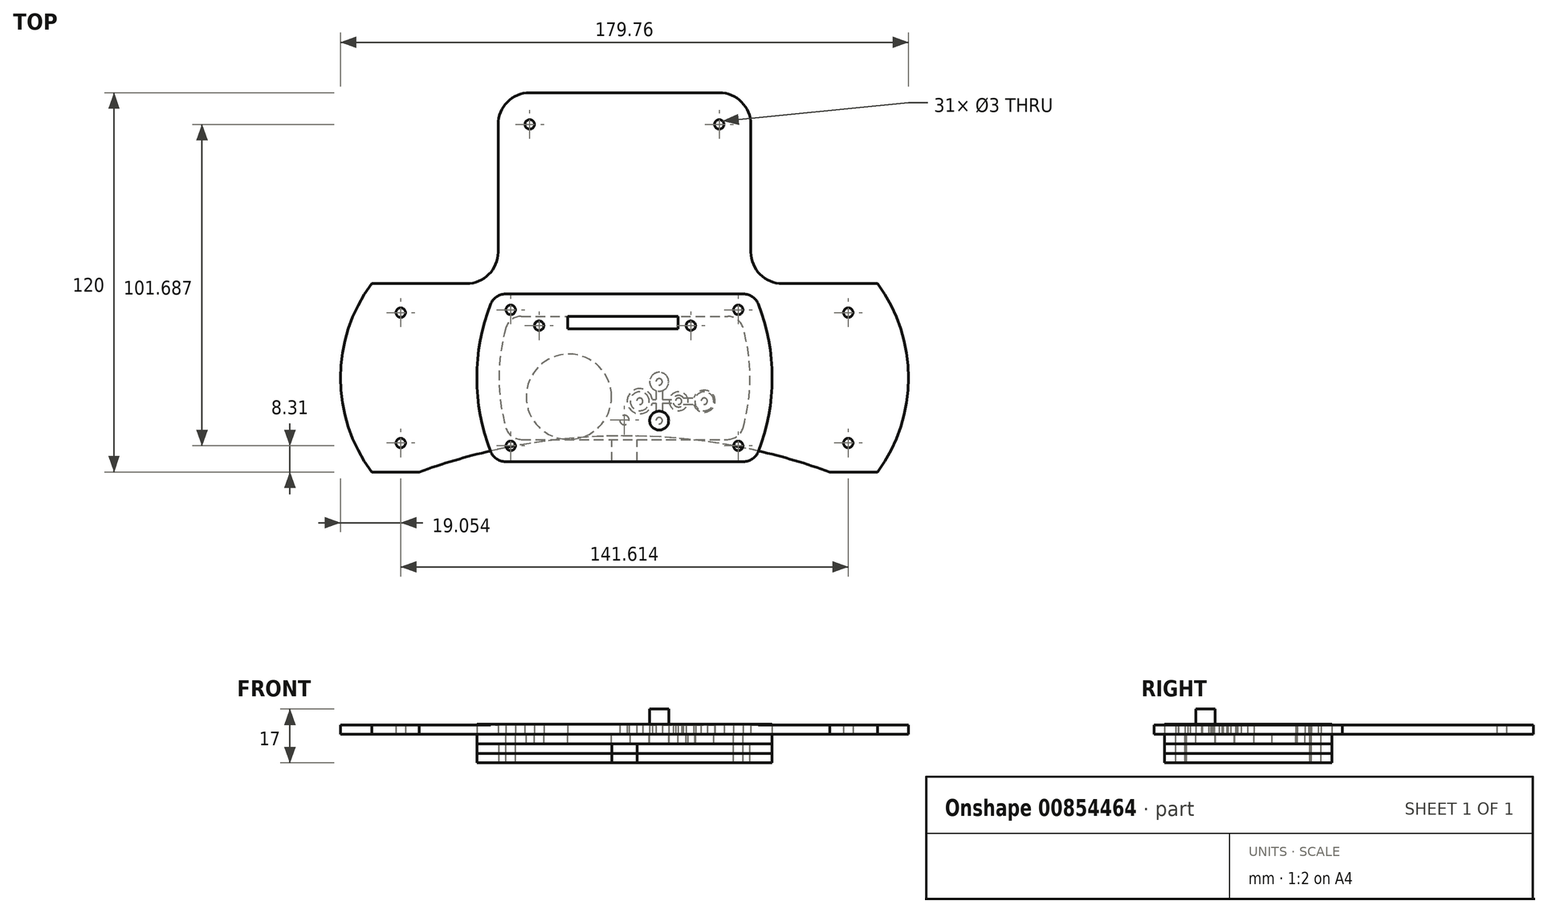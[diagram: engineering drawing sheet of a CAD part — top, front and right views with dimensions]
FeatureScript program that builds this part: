
annotation { "Feature Type Name" : "Feature", "Feature Type Description" : "" }
export const myFeature = defineFeature(function(context is Context, id is Id, definition is map)
    precondition{}
    {
        {
            var Q0;
            Q0=qCreatedBy(makeId("Top.planeOp"),FACE);
            var sketch = newSketch(context, id + "F0", { "sketchPlane" : qUnion([Q0])});
            skLineSegment(sketch, "E0.bottom", {"start": v(80.04, -29.81) * mm, "end": v(65, -29.81) * mm});
            skLineSegment(sketch, "E0.top", {"start": v(80.04, 29.81) * mm, "end": v(50, 29.81) * mm});
            skPoint(sketch, "E0.middle", {"position": v(0, 0) * mm});
            skLineSegment(sketch, "E1.top", {"start": v(30, 90.19) * mm, "end": v(-30, 90.19) * mm});
            skLineSegment(sketch, "E1.left", {"start": v(40, 39.81) * mm, "end": v(40, 80.19) * mm});
            skLineSegment(sketch, "E1.right", {"start": v(-40, 39.81) * mm, "end": v(-40, 80.19) * mm});
            skPoint(sketch, "E1.middle", {"position": v(0, 60) * mm});
            skPoint(sketch, "E2.visualSharp", {"position": v(-40, 29.81) * mm});
            skPoint(sketch, "E3.visualSharp", {"position": v(-40, 90.19) * mm});
            skPoint(sketch, "E4.visualSharp", {"position": v(40, 90.19) * mm});
            skPoint(sketch, "E5.visualSharp", {"position": v(40, 29.81) * mm});
            skPoint(sketch, "E6.visualSharp", {"position": v(80, 29.81) * mm});
            skPoint(sketch, "E7", {"position": v(-65, -29.81) * mm});
            skPoint(sketch, "E8", {"position": v(65, -29.81) * mm});
            skArc(sketch, "E9", {"start": v(65, -29.81) * mm, "mid": v(0, -18.35) * mm, "end": v(-65, -29.81) * mm});
            skPoint(sketch, "E10.visualSharp", {"position": v(-80, -29.81) * mm});
            skPoint(sketch, "E11.visualSharp", {"position": v(80, -29.81) * mm});
            skPoint(sketch, "E12.visualSharp", {"position": v(-80, 29.81) * mm});
            skLineSegment(sketch, "E13.trimOffspring", {"start": v(-65, -29.81) * mm, "end": v(-80, -29.81) * mm});
            skLineSegment(sketch, "E14.trimOffspring", {"start": v(-50, 29.81) * mm, "end": v(-80, 29.81) * mm});
            skArc(sketch, "E15.filletArc", {"start": v(-50, 29.81) * mm, "mid": v(-42.93, 32.74) * mm, "end": v(-40, 39.81) * mm});
            skArc(sketch, "E16.filletArc", {"start": v(40, 39.81) * mm, "mid": v(42.93, 32.74) * mm, "end": v(50, 29.81) * mm});
            skArc(sketch, "E17.filletArc", {"start": v(-30, 90.19) * mm, "mid": v(-37.07, 87.26) * mm, "end": v(-40, 80.19) * mm});
            skArc(sketch, "E18.filletArc", {"start": v(40, 80.19) * mm, "mid": v(37.07, 87.26) * mm, "end": v(30, 90.19) * mm});
            skArc(sketch, "E19", {"start": v(-80, 29.81) * mm, "mid": v(-89.86, 0) * mm, "end": v(-80, -29.81) * mm});
            skArc(sketch, "E20.MirrorCS", {"start": v(80, 29.87) * mm, "mid": v(89.9, 0) * mm, "end": v(80, -29.87) * mm});
            skLineSegment(sketch, "E21", {"start": v(0, 90.19) * mm, "end": v(0, 0) * mm, "construction": true});
            skCircle(sketch, "E22", {"center": v(-30, 80.19) * mm, "radius": 1.5 * mm});
            skCircle(sketch, "E23", {"center": v(30, 80.19) * mm, "radius": 1.5 * mm});
            skCircle(sketch, "E24", {"center": v(-70.8, 20.62) * mm, "radius": 1.5 * mm});
            skLineSegment(sketch, "E25", {"start": v(-80, 29.81) * mm, "end": v(-70.8, 20.62) * mm, "construction": true});
            skLineSegment(sketch, "E26.MirrorCS", {"start": v(80, 29.81) * mm, "end": v(70.8, 20.62) * mm, "construction": true});
            skCircle(sketch, "E27.MirrorC", {"center": v(70.8, 20.62) * mm, "radius": 1.5 * mm});
            skLineSegment(sketch, "E28", {"start": v(0, 0) * mm, "end": v(-39.86, 0) * mm, "construction": true});
            skLineSegment(sketch, "E29.MirrorCS", {"start": v(0, 0) * mm, "end": v(39.86, 0) * mm, "construction": true});
            skLineSegment(sketch, "E30.MirrorCS", {"start": v(80, -29.8) * mm, "end": v(70.8, -20.61) * mm, "construction": true});
            skCircle(sketch, "E31.MirrorC", {"center": v(70.8, -20.61) * mm, "radius": 1.5 * mm});
            skLineSegment(sketch, "E32.MirrorCS", {"start": v(-80, -29.82) * mm, "end": v(-70.8, -20.63) * mm, "construction": true});
            skCircle(sketch, "E33.MirrorC", {"center": v(-70.8, -20.63) * mm, "radius": 1.5 * mm});
            skLineSegment(sketch, "E34", {"start": v(0, -18.35) * mm, "end": v(0, -13.35) * mm, "construction": true});
            skCircle(sketch, "E35", {"center": v(0, -13.35) * mm, "radius": 1.5 * mm});
            skSolve(sketch);
        }
        {
            var Q0;
            Q0=qCreatedBy(makeId("Top.planeOp"),FACE);
            var sketch = newSketch(context, id + "F1", { "sketchPlane" : qUnion([Q0])});
            skLineSegment(sketch, "E36.bottom", {"start": v(36, -21.5) * mm, "end": v(-36, -21.5) * mm, "construction": true});
            skLineSegment(sketch, "E36.top", {"start": v(36, 21.5) * mm, "end": v(-36, 21.5) * mm, "construction": true});
            skLineSegment(sketch, "E36.left", {"start": v(36, -21.5) * mm, "end": v(36, 21.5) * mm, "construction": true});
            skLineSegment(sketch, "E36.right", {"start": v(-36, -21.5) * mm, "end": v(-36, 21.5) * mm, "construction": true});
            skPoint(sketch, "E36.middle", {"position": v(0, 0) * mm});
            skLineSegment(sketch, "E37", {"start": v(-36, -6) * mm, "end": v(-17.6, -6) * mm, "construction": true});
            skLineSegment(sketch, "E38", {"start": v(-17.6, -6) * mm, "end": v(-17.6, -21.5) * mm, "construction": true});
            skCircle(sketch, "E39", {"center": v(-17.6, -6) * mm, "radius": 13.5 * mm});
            skCircle(sketch, "E40", {"center": v(4.84, -7.4) * mm, "radius": 3 * mm});
            skCircle(sketch, "E41", {"center": v(17.14, -7.4) * mm, "radius": 3 * mm});
            skCircle(sketch, "E42", {"center": v(10.99, -13.55) * mm, "radius": 3 * mm});
            skCircle(sketch, "E43", {"center": v(25.23, -7.4) * mm, "radius": 3 * mm});
            skCircle(sketch, "E44", {"center": v(10.99, -1.25) * mm, "radius": 3 * mm});
            skLineSegment(sketch, "E45", {"start": v(4.84, -7.4) * mm, "end": v(17.14, -7.4) * mm, "construction": true});
            skLineSegment(sketch, "E46", {"start": v(10.99, -1.25) * mm, "end": v(10.99, -13.55) * mm, "construction": true});
            skLineSegment(sketch, "E47", {"start": v(17.14, -7.4) * mm, "end": v(25.23, -7.4) * mm, "construction": true});
            skPoint(sketch, "E48", {"position": v(10.99, -7.4) * mm});
            skLineSegment(sketch, "E49.0", {"start": v(37.68, 26.5) * mm, "end": v(-37.68, 26.5) * mm});
            skLineSegment(sketch, "E49.1", {"start": v(41, -26.5) * mm, "end": v(41, 26.5) * mm, "construction": true});
            skLineSegment(sketch, "E49.2", {"start": v(37.68, -26.5) * mm, "end": v(-37.68, -26.5) * mm});
            skLineSegment(sketch, "E49.3", {"start": v(-41, -26.5) * mm, "end": v(-41, 26.5) * mm, "construction": true});
            skArc(sketch, "E50", {"start": v(42.34, -23.32) * mm, "mid": v(46.73, 0) * mm, "end": v(42.34, 23.32) * mm});
            skLineSegment(sketch, "E51", {"start": v(0, 21.5) * mm, "end": v(0, 0) * mm, "construction": true});
            skArc(sketch, "E52.MirrorCS", {"start": v(-42.34, -23.32) * mm, "mid": v(-46.73, 0) * mm, "end": v(-42.34, 23.32) * mm});
            skPoint(sketch, "E53.visualSharp", {"position": v(-41, 26.5) * mm});
            skArc(sketch, "E53.filletArc", {"start": v(-37.68, 26.5) * mm, "mid": v(-40.5, 25.63) * mm, "end": v(-42.34, 23.32) * mm});
            skPoint(sketch, "E54.visualSharp", {"position": v(41, 26.5) * mm});
            skArc(sketch, "E54.filletArc", {"start": v(42.34, 23.32) * mm, "mid": v(40.5, 25.63) * mm, "end": v(37.68, 26.5) * mm});
            skPoint(sketch, "E55.visualSharp", {"position": v(41, -26.5) * mm});
            skArc(sketch, "E55.filletArc", {"start": v(37.68, -26.5) * mm, "mid": v(40.5, -25.63) * mm, "end": v(42.34, -23.32) * mm});
            skPoint(sketch, "E56.visualSharp", {"position": v(-41, -26.5) * mm});
            skArc(sketch, "E56.filletArc", {"start": v(-42.34, -23.32) * mm, "mid": v(-40.5, -25.63) * mm, "end": v(-37.68, -26.5) * mm});
            skLineSegment(sketch, "E57", {"start": v(-27, 21.5) * mm, "end": v(-27, 16.5) * mm, "construction": true});
            skLineSegment(sketch, "E58", {"start": v(21, 21.5) * mm, "end": v(21, 16.5) * mm, "construction": true});
            skLineSegment(sketch, "E59", {"start": v(21, 16.5) * mm, "end": v(36, 16.5) * mm, "construction": true});
            skLineSegment(sketch, "E60", {"start": v(-27, 16.5) * mm, "end": v(-36, 16.5) * mm, "construction": true});
            skCircle(sketch, "E61", {"center": v(-27, 16.5) * mm, "radius": 1.5 * mm});
            skCircle(sketch, "E62", {"center": v(21, 16.5) * mm, "radius": 1.5 * mm});
            skCircle(sketch, "E63", {"center": v(-36, 21.5) * mm, "radius": 1.5 * mm});
            skCircle(sketch, "E64", {"center": v(36, 21.5) * mm, "radius": 1.5 * mm});
            skCircle(sketch, "E65", {"center": v(36, -21.5) * mm, "radius": 1.5 * mm});
            skCircle(sketch, "E66", {"center": v(-36, -21.5) * mm, "radius": 1.5 * mm});
            skLineSegment(sketch, "E67.bottom", {"start": v(-18, 19.49) * mm, "end": v(17, 19.49) * mm});
            skLineSegment(sketch, "E67.top", {"start": v(-18, 15.49) * mm, "end": v(17, 15.49) * mm});
            skLineSegment(sketch, "E67.left", {"start": v(-18, 19.49) * mm, "end": v(-18, 15.49) * mm});
            skLineSegment(sketch, "E67.right", {"start": v(17, 19.49) * mm, "end": v(17, 15.49) * mm});
            skLineSegment(sketch, "E68", {"start": v(1.84, -7.4) * mm, "end": v(-4.16, -7.4) * mm, "construction": true});
            skLineSegment(sketch, "E69", {"start": v(10.43, -16.5) * mm, "end": v(10.43, -21.5) * mm, "construction": true});
            skSolve(sketch);
        }
        {
            var Q0;
            Q0 = qSketchRegion(id + "F0", true);
            extrude(context, id + "F2", {"entities" : qUnion([Q0]), "depth" : 3 * mm, "offsetDistance" : 25 * mm});
        }
        {
            var Q0;
            Q0=makeQuery(id+"F1.imprint","IMPRINT",FACE,{"disambiguationData":[TD([[makeQuery(id+"F1.imprint","IMPRINT",EDGE,{"derivedFrom":sQuery(id+"F1.wireOp",EDGE,"E39")}),-1.0]])]});
            extrude(context, id + "F3", {"entities" : qUnion([Q0]), "oppositeDirection" : true, "depth" : 3 * mm, "offsetDistance" : 25 * mm});
        }
        {
            var Q0;
            Q0=makeQuery(id+"F3.opExtrude","CAP_FACE",FACE,{"disambiguationData":[OSD([sQuery(id+"F1.wireOp",EDGE,"E39"),sQuery(id+"F1.wireOp",EDGE,"E40"),sQuery(id+"F1.wireOp",EDGE,"E41"),sQuery(id+"F1.wireOp",EDGE,"E42"),sQuery(id+"F1.wireOp",EDGE,"E43"),sQuery(id+"F1.wireOp",EDGE,"E44"),sQuery(id+"F1.wireOp",EDGE,"E49.0"),sQuery(id+"F1.wireOp",EDGE,"E49.2"),sQuery(id+"F1.wireOp",EDGE,"E50"),sQuery(id+"F1.wireOp",EDGE,"E52.MirrorCS"),sQuery(id+"F1.wireOp",EDGE,"E53.filletArc"),sQuery(id+"F1.wireOp",EDGE,"E54.filletArc"),sQuery(id+"F1.wireOp",EDGE,"E55.filletArc"),sQuery(id+"F1.wireOp",EDGE,"E56.filletArc"),sQuery(id+"F1.wireOp",EDGE,"E61"),sQuery(id+"F1.wireOp",EDGE,"E62"),sQuery(id+"F1.wireOp",EDGE,"E63"),sQuery(id+"F1.wireOp",EDGE,"E64"),sQuery(id+"F1.wireOp",EDGE,"E65"),sQuery(id+"F1.wireOp",EDGE,"E66")])],"isStart":false});
            var sketch = newSketch(context, id + "F4", { "sketchPlane" : qUnion([Q0])});
            skLineSegment(sketch, "E70", {"start": v(-37.68, -26.5) * mm, "end": v(37.68, -26.5) * mm});
            skArc(sketch, "E71", {"start": v(37.68, -26.5) * mm, "mid": v(40.5, -25.63) * mm, "end": v(42.34, -23.32) * mm});
            skArc(sketch, "E72", {"start": v(42.34, 23.32) * mm, "mid": v(40.5, 25.63) * mm, "end": v(37.68, 26.5) * mm});
            skArc(sketch, "E73", {"start": v(42.34, -23.32) * mm, "mid": v(46.73, 0) * mm, "end": v(42.34, 23.32) * mm});
            skLineSegment(sketch, "E74", {"start": v(0, 26.5) * mm, "end": v(0, 0) * mm, "construction": true});
            skArc(sketch, "E75.MirrorCS", {"start": v(-42.34, -23.32) * mm, "mid": v(-46.73, 0) * mm, "end": v(-42.34, 23.32) * mm});
            skArc(sketch, "E76.MirrorCS", {"start": v(-42.34, 23.32) * mm, "mid": v(-40.5, 25.63) * mm, "end": v(-37.68, 26.5) * mm});
            skArc(sketch, "E77.MirrorCS", {"start": v(-37.68, -26.5) * mm, "mid": v(-40.5, -25.63) * mm, "end": v(-42.34, -23.32) * mm});
            skArc(sketch, "E78.1", {"start": v(-37.48, -15.9) * mm, "mid": v(-39.73, 0) * mm, "end": v(-37.48, 15.9) * mm});
            skLineSegment(sketch, "E78.2", {"start": v(-32.67, -19.5) * mm, "end": v(32.67, -19.5) * mm});
            skArc(sketch, "E78.3", {"start": v(37.48, -15.9) * mm, "mid": v(39.73, 0) * mm, "end": v(37.48, 15.9) * mm});
            skPoint(sketch, "E79.visualSharp", {"position": v(-36.3, 19.5) * mm});
            skArc(sketch, "E79.filletArc", {"start": v(-32.67, 19.5) * mm, "mid": v(-35.68, 18.5) * mm, "end": v(-37.48, 15.9) * mm});
            skPoint(sketch, "E80.visualSharp", {"position": v(36.3, 19.5) * mm});
            skArc(sketch, "E80.filletArc", {"start": v(37.48, 15.9) * mm, "mid": v(35.68, 18.5) * mm, "end": v(32.67, 19.5) * mm});
            skPoint(sketch, "E81.visualSharp", {"position": v(-36.3, -19.5) * mm});
            skArc(sketch, "E81.filletArc", {"start": v(-37.48, -15.9) * mm, "mid": v(-35.68, -18.5) * mm, "end": v(-32.67, -19.5) * mm});
            skPoint(sketch, "E82.visualSharp", {"position": v(36.3, -19.5) * mm});
            skArc(sketch, "E82.filletArc", {"start": v(32.67, -19.5) * mm, "mid": v(35.68, -18.5) * mm, "end": v(37.48, -15.9) * mm});
            skCircle(sketch, "E83", {"center": v(-36, 21.5) * mm, "radius": 1.5 * mm});
            skCircle(sketch, "E84", {"center": v(36, 21.5) * mm, "radius": 1.5 * mm});
            skCircle(sketch, "E85", {"center": v(36, -21.5) * mm, "radius": 1.5 * mm});
            skCircle(sketch, "E86", {"center": v(-36, -21.5) * mm, "radius": 1.5 * mm});
            skLineSegment(sketch, "E87", {"start": v(-4, 26.5) * mm, "end": v(-4, 19.5) * mm});
            skLineSegment(sketch, "E88.MirrorCS", {"start": v(4, 26.5) * mm, "end": v(4, 19.5) * mm});
            skLineSegment(sketch, "E89.trimOffspring", {"start": v(4, 26.5) * mm, "end": v(37.68, 26.5) * mm});
            skLineSegment(sketch, "E90.trimOffspring", {"start": v(4, 19.5) * mm, "end": v(32.67, 19.5) * mm});
            skLineSegment(sketch, "E91", {"start": v(-37.68, 26.5) * mm, "end": v(-4, 26.5) * mm});
            skLineSegment(sketch, "E92", {"start": v(-32.67, 19.5) * mm, "end": v(-4, 19.5) * mm});
            skLineSegment(sketch, "E93", {"start": v(-4, 19.5) * mm, "end": v(4, 19.5) * mm});
            skLineSegment(sketch, "E94", {"start": v(-4, 26.5) * mm, "end": v(4, 26.5) * mm});
            skSolve(sketch);
        }
        {
            var Q0;
            Q0=makeQuery(id+"F4.imprint","IMPRINT",FACE,{"disambiguationData":[TD([[makeQuery(id+"F4.imprint","IMPRINT",EDGE,{"derivedFrom":sQuery(id+"F4.wireOp",EDGE,"E70")}),-1.0]])]});
            extrude(context, id + "F5", {"entities" : qUnion([Q0]), "depth" : 3 * mm, "offsetDistance" : 25 * mm});
        }
        {
            var Q0;
            Q0=makeQuery(id+"F1.imprint","IMPRINT",FACE,{"disambiguationData":[TD([[makeQuery(id+"F1.imprint","IMPRINT",EDGE,{"derivedFrom":sQuery(id+"F1.wireOp",EDGE,"E39")}),-1.0]])]});
            var sketch = newSketch(context, id + "F6", { "sketchPlane" : qUnion([Q0])});
            skArc(sketch, "E95", {"start": v(11.99, -4.08) * mm, "mid": v(10.99, 1.75) * mm, "end": v(9.99, -4.08) * mm});
            skArc(sketch, "E96", {"start": v(8.77, -6.8) * mm, "mid": v(0.85, -7.4) * mm, "end": v(8.77, -8.01) * mm});
            skArc(sketch, "E97", {"start": v(9.99, -10.72) * mm, "mid": v(10.99, -16.55) * mm, "end": v(11.99, -10.72) * mm});
            skArc(sketch, "E98", {"start": v(15.41, -8.01) * mm, "mid": v(16.92, -9.21) * mm, "end": v(18.66, -8.4) * mm});
            skArc(sketch, "E99", {"start": v(21.9, -8.4) * mm, "mid": v(28.7, -7.4) * mm, "end": v(21.9, -6.4) * mm});
            skLineSegment(sketch, "E100.0", {"start": v(8.77, -8.01) * mm, "end": v(9.99, -8.01) * mm});
            skLineSegment(sketch, "E101.0", {"start": v(9.99, -4.08) * mm, "end": v(9.99, -6.8) * mm});
            skLineSegment(sketch, "E102.MirrorCS", {"start": v(11.99, -4.08) * mm, "end": v(11.99, -6.8) * mm});
            skLineSegment(sketch, "E103.MirrorCS", {"start": v(8.77, -6.8) * mm, "end": v(9.99, -6.8) * mm});
            skPoint(sketch, "E104.orphan", {"position": v(11.99, -1.25) * mm});
            skPoint(sketch, "E105.orphan", {"position": v(9.99, -1.25) * mm});
            skLineSegment(sketch, "E106.trimOffspring", {"start": v(11.99, -6.8) * mm, "end": v(15.41, -6.8) * mm});
            skLineSegment(sketch, "E107.trimOffspring", {"start": v(11.99, -8.01) * mm, "end": v(11.99, -10.72) * mm});
            skLineSegment(sketch, "E108.trimOffspring", {"start": v(9.99, -8.01) * mm, "end": v(9.99, -10.72) * mm});
            skPoint(sketch, "E109.orphan", {"position": v(18.24, -6.8) * mm});
            skPoint(sketch, "E110.orphan", {"position": v(18.24, -8.01) * mm});
            skLineSegment(sketch, "E111.trimOffspring", {"start": v(11.99, -8.01) * mm, "end": v(15.41, -8.01) * mm});
            skPoint(sketch, "E112.orphan", {"position": v(11.99, -13.55) * mm});
            skPoint(sketch, "E113.orphan", {"position": v(9.99, -13.55) * mm});
            skLineSegment(sketch, "E114.0", {"start": v(18.66, -8.4) * mm, "end": v(21.9, -8.4) * mm});
            skLineSegment(sketch, "E115.MirrorCS", {"start": v(18.66, -6.4) * mm, "end": v(21.9, -6.4) * mm});
            skPoint(sketch, "E116.orphan", {"position": v(15.83, -6.4) * mm});
            skPoint(sketch, "E117.orphan", {"position": v(15.83, -8.4) * mm});
            skArc(sketch, "E118.trimOffspring", {"start": v(18.66, -6.4) * mm, "mid": v(16.92, -5.6) * mm, "end": v(15.41, -6.8) * mm});
            skPoint(sketch, "E119.orphan", {"position": v(24.73, -6.4) * mm});
            skPoint(sketch, "E120.orphan", {"position": v(24.73, -8.4) * mm});
            skCircle(sketch, "E121", {"center": v(4.84, -7.4) * mm, "radius": 1 * mm});
            skCircle(sketch, "E122", {"center": v(10.99, -1.25) * mm, "radius": 1 * mm});
            skCircle(sketch, "E123", {"center": v(10.99, -13.55) * mm, "radius": 1 * mm});
            skCircle(sketch, "E124", {"center": v(17.14, -7.4) * mm, "radius": 1 * mm});
            skCircle(sketch, "E125", {"center": v(25.23, -7.4) * mm, "radius": 1 * mm});
            skSolve(sketch);
        }
        {
            var Q0;
            Q0 = qSketchRegion(id + "F6", true);
            extrude(context, id + "F7", {"entities" : qUnion([Q0]), "depth" : 3 * mm, "offsetDistance" : 25 * mm});
        }
        {
            var Q0;
            Q0=makeQuery(id+"F7.opExtrude","CAP_FACE",FACE,{"disambiguationData":[OSD([sQuery(id+"F6.wireOp",EDGE,"E95"),sQuery(id+"F6.wireOp",EDGE,"E96"),sQuery(id+"F6.wireOp",EDGE,"E97"),sQuery(id+"F6.wireOp",EDGE,"E98"),sQuery(id+"F6.wireOp",EDGE,"E99"),sQuery(id+"F6.wireOp",EDGE,"E100.0"),sQuery(id+"F6.wireOp",EDGE,"E101.0"),sQuery(id+"F6.wireOp",EDGE,"E102.MirrorCS"),sQuery(id+"F6.wireOp",EDGE,"E103.MirrorCS"),sQuery(id+"F6.wireOp",EDGE,"E106.trimOffspring"),sQuery(id+"F6.wireOp",EDGE,"E107.trimOffspring"),sQuery(id+"F6.wireOp",EDGE,"E108.trimOffspring"),sQuery(id+"F6.wireOp",EDGE,"E111.trimOffspring"),sQuery(id+"F6.wireOp",EDGE,"E114.0"),sQuery(id+"F6.wireOp",EDGE,"E115.MirrorCS"),sQuery(id+"F6.wireOp",EDGE,"E118.trimOffspring"),sQuery(id+"F6.wireOp",EDGE,"E121"),sQuery(id+"F6.wireOp",EDGE,"E122"),sQuery(id+"F6.wireOp",EDGE,"E123"),sQuery(id+"F6.wireOp",EDGE,"E124"),sQuery(id+"F6.wireOp",EDGE,"E125")])],"isStart":false});
            var sketch = newSketch(context, id + "F8", { "sketchPlane" : qUnion([Q0])});
            skCircle(sketch, "E126", {"center": v(10.99, -13.55) * mm, "radius": 3 * mm});
            skSolve(sketch);
        }
        {
            var Q0;
            Q0 = qSketchRegion(id + "F8", true);
            extrude(context, id + "F9", {"entities" : qUnion([Q0]), "depth" : 5 * mm, "offsetDistance" : 25 * mm});
        }
        {
            var Q0;
            Q0=makeQuery(id+"F1.imprint","IMPRINT",FACE,{"disambiguationData":[TD([[makeQuery(id+"F1.imprint","IMPRINT",EDGE,{"derivedFrom":sQuery(id+"F1.wireOp",EDGE,"E40")}),1.0]])]});
            var Q1;
            Q1=makeQuery(id+"F1.imprint","IMPRINT",FACE,{"disambiguationData":[TD([[makeQuery(id+"F1.imprint","IMPRINT",EDGE,{"derivedFrom":sQuery(id+"F1.wireOp",EDGE,"E44")}),1.0]])]});
            var Q2;
            Q2=makeQuery(id+"F1.imprint","IMPRINT",FACE,{"disambiguationData":[TD([[makeQuery(id+"F1.imprint","IMPRINT",EDGE,{"derivedFrom":sQuery(id+"F1.wireOp",EDGE,"E41")}),1.0]])]});
            var Q3;
            Q3=makeQuery(id+"F1.imprint","IMPRINT",FACE,{"disambiguationData":[TD([[makeQuery(id+"F1.imprint","IMPRINT",EDGE,{"derivedFrom":sQuery(id+"F1.wireOp",EDGE,"E42")}),1.0]])]});
            var Q4;
            Q4=makeQuery(id+"F1.imprint","IMPRINT",FACE,{"disambiguationData":[TD([[makeQuery(id+"F1.imprint","IMPRINT",EDGE,{"derivedFrom":sQuery(id+"F1.wireOp",EDGE,"E43")}),1.0]])]});
            var Q5;
            Q5=makeQuery(id+"F1.imprint","IMPRINT",FACE,{"disambiguationData":[TD([[makeQuery(id+"F1.imprint","IMPRINT",EDGE,{"derivedFrom":sQuery(id+"F1.wireOp",EDGE,"E39")}),-1.0]])]});
            var Q6;
            Q6=makeQuery(id+"F1.imprint","IMPRINT",FACE,{"disambiguationData":[TD([[makeQuery(id+"F1.imprint","IMPRINT",EDGE,{"derivedFrom":sQuery(id+"F1.wireOp",EDGE,"E39")}),1.0]])]});
            extrude(context, id + "F10", {"entities" : qUnion([Q0, Q1, Q2, Q3, Q4, Q5, Q6]), "depth" : 3.2 * mm, "offsetDistance" : 25 * mm});
        }
        {
            var Q0;
            Q0 = qSketchRegion(id + "F4", true);
            var Q1;
            Q1=makeQuery(id+"F5.opExtrude","CAP_FACE",FACE,{"disambiguationData":[OSD([sQuery(id+"F4.wireOp",EDGE,"E70"),sQuery(id+"F4.wireOp",EDGE,"E71"),sQuery(id+"F4.wireOp",EDGE,"E72"),sQuery(id+"F4.wireOp",EDGE,"E73"),sQuery(id+"F4.wireOp",EDGE,"E75.MirrorCS"),sQuery(id+"F4.wireOp",EDGE,"E76.MirrorCS"),sQuery(id+"F4.wireOp",EDGE,"E77.MirrorCS"),sQuery(id+"F4.wireOp",EDGE,"E78.1"),sQuery(id+"F4.wireOp",EDGE,"E78.2"),sQuery(id+"F4.wireOp",EDGE,"E78.3"),sQuery(id+"F4.wireOp",EDGE,"E79.filletArc"),sQuery(id+"F4.wireOp",EDGE,"E80.filletArc"),sQuery(id+"F4.wireOp",EDGE,"E81.filletArc"),sQuery(id+"F4.wireOp",EDGE,"E82.filletArc"),sQuery(id+"F4.wireOp",EDGE,"E83"),sQuery(id+"F4.wireOp",EDGE,"E84"),sQuery(id+"F4.wireOp",EDGE,"E85"),sQuery(id+"F4.wireOp",EDGE,"E86"),sQuery(id+"F4.wireOp",EDGE,"E89.trimOffspring"),sQuery(id+"F4.wireOp",EDGE,"E90.trimOffspring"),sQuery(id+"F4.wireOp",EDGE,"E91"),sQuery(id+"F4.wireOp",EDGE,"E92"),sQuery(id+"F4.wireOp",EDGE,"E93"),sQuery(id+"F4.wireOp",EDGE,"E94")])],"isStart":false});
            extrude(context, id + "F11", {"entities" : qUnion([Q0, Q1]), "depth" : 3 * mm, "offsetDistance" : 25 * mm});
        }
    });
